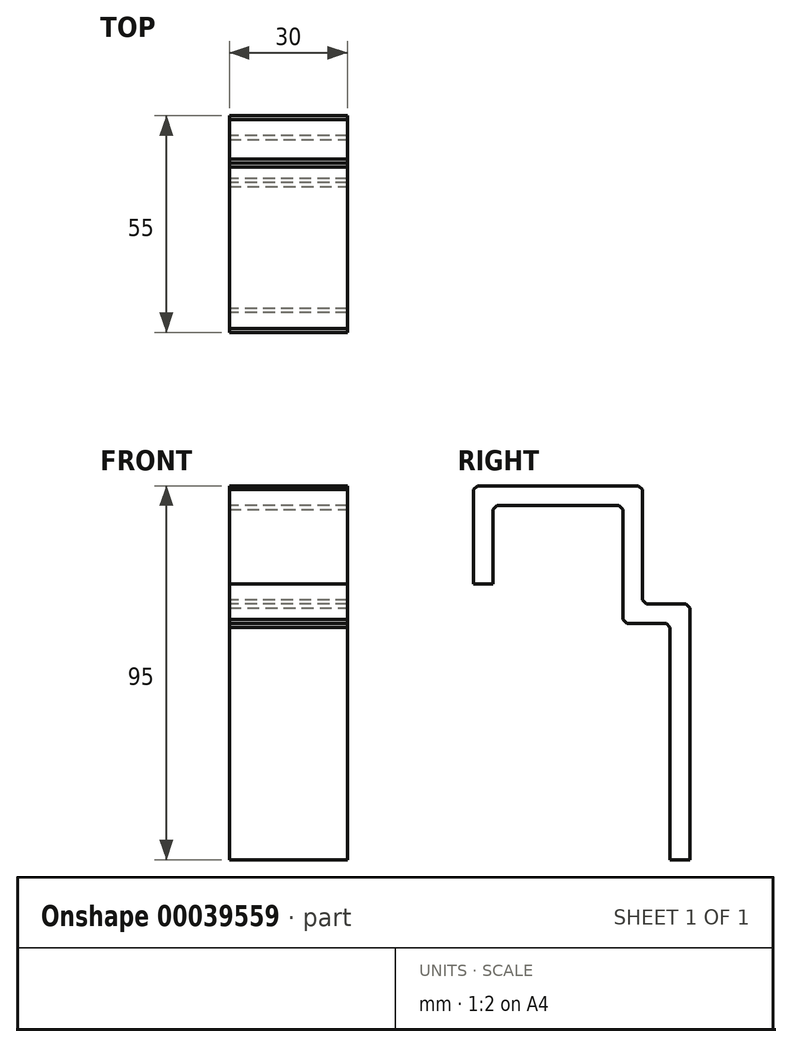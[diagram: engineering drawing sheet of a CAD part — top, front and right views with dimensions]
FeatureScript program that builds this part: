
annotation { "Feature Type Name" : "Feature", "Feature Type Description" : "" }
export const myFeature = defineFeature(function(context is Context, id is Id, definition is map)
    precondition{}
    {
        {
            var Q0;
            Q0=qCreatedBy(makeId("Right.planeOp"),FACE);
            var sketch = newSketch(context, id + "F0", { "sketchPlane" : qUnion([Q0])});
            skLineSegment(sketch, "E0", {"start": v(0, 0) * mm, "end": v(0, 65) * mm});
            skLineSegment(sketch, "E1", {"start": v(0, 65) * mm, "end": v(-12, 65) * mm});
            skLineSegment(sketch, "E2", {"start": v(-12, 65) * mm, "end": v(-12, 95) * mm});
            skLineSegment(sketch, "E3", {"start": v(-12, 95) * mm, "end": v(-55, 95) * mm});
            skLineSegment(sketch, "E4", {"start": v(-55, 95) * mm, "end": v(-55, 70) * mm});
            skLineSegment(sketch, "E5.0", {"start": v(-50, 90) * mm, "end": v(-50, 70) * mm});
            skLineSegment(sketch, "E5.1", {"start": v(-5, 0) * mm, "end": v(-5, 60) * mm});
            skLineSegment(sketch, "E5.2", {"start": v(-5, 60) * mm, "end": v(-17, 60) * mm});
            skLineSegment(sketch, "E5.3", {"start": v(-17, 60) * mm, "end": v(-17, 90) * mm});
            skLineSegment(sketch, "E5.4", {"start": v(-17, 90) * mm, "end": v(-50, 90) * mm});
            skLineSegment(sketch, "E6", {"start": v(-50, 70) * mm, "end": v(-55, 70) * mm});
            skLineSegment(sketch, "E7", {"start": v(-5, 0) * mm, "end": v(0, 0) * mm});
            skSolve(sketch);
        }
        {
            var Q0;
            Q0=makeQuery(id+"F0.imprint","IMPRINT",FACE,{"disambiguationData":[TD([[makeQuery(id+"F0.imprint","IMPRINT",EDGE,{"derivedFrom":sQuery(id+"F0.wireOp",EDGE,"E0")}),1.0]])]});
            extrude(context, id + "F1", {"entities" : qUnion([Q0]), "depth" : 30 * mm});
        }
        {
            var Q0;
            Q0=makeQuery(id+"F1.opExtrude","SWEPT_EDGE",EDGE,{"disambiguationData":[OSD([sQuery(id+"F0.wireOp",EDGE,"E5.2"),sQuery(id+"F0.wireOp",EDGE,"E5.3")])]});
            var Q1;
            Q1=makeQuery(id+"F1.opExtrude","SWEPT_EDGE",EDGE,{"disambiguationData":[OSD([sQuery(id+"F0.wireOp",EDGE,"E1"),sQuery(id+"F0.wireOp",EDGE,"E2")])]});
            var Q2;
            Q2=makeQuery(id+"F1.opExtrude","SWEPT_EDGE",EDGE,{"disambiguationData":[OSD([sQuery(id+"F0.wireOp",EDGE,"E0"),sQuery(id+"F0.wireOp",EDGE,"E1")])]});
            var Q3;
            Q3=makeQuery(id+"F1.opExtrude","SWEPT_EDGE",EDGE,{"disambiguationData":[OSD([sQuery(id+"F0.wireOp",EDGE,"E2"),sQuery(id+"F0.wireOp",EDGE,"E3")])]});
            var Q4;
            Q4=makeQuery(id+"F1.opExtrude","SWEPT_EDGE",EDGE,{"disambiguationData":[OSD([sQuery(id+"F0.wireOp",EDGE,"E3"),sQuery(id+"F0.wireOp",EDGE,"E4")])]});
            var Q5;
            Q5=makeQuery(id+"F1.opExtrude","SWEPT_EDGE",EDGE,{"disambiguationData":[OSD([sQuery(id+"F0.wireOp",EDGE,"E5.1"),sQuery(id+"F0.wireOp",EDGE,"E5.2")])]});
            var Q6;
            Q6=makeQuery(id+"F1.opExtrude","SWEPT_EDGE",EDGE,{"disambiguationData":[OSD([sQuery(id+"F0.wireOp",EDGE,"E5.3"),sQuery(id+"F0.wireOp",EDGE,"E5.4")])]});
            var Q7;
            Q7=makeQuery(id+"F1.opExtrude","SWEPT_EDGE",EDGE,{"disambiguationData":[OSD([sQuery(id+"F0.wireOp",EDGE,"E5.0"),sQuery(id+"F0.wireOp",EDGE,"E5.4")])]});
            chamfer(context, id + "F2", {"entities" : qUnion([Q0, Q1, Q2, Q3, Q4, Q5, Q6, Q7]), "width" : 1 * mm, "tangentPropagation" : true});
        }
    });
